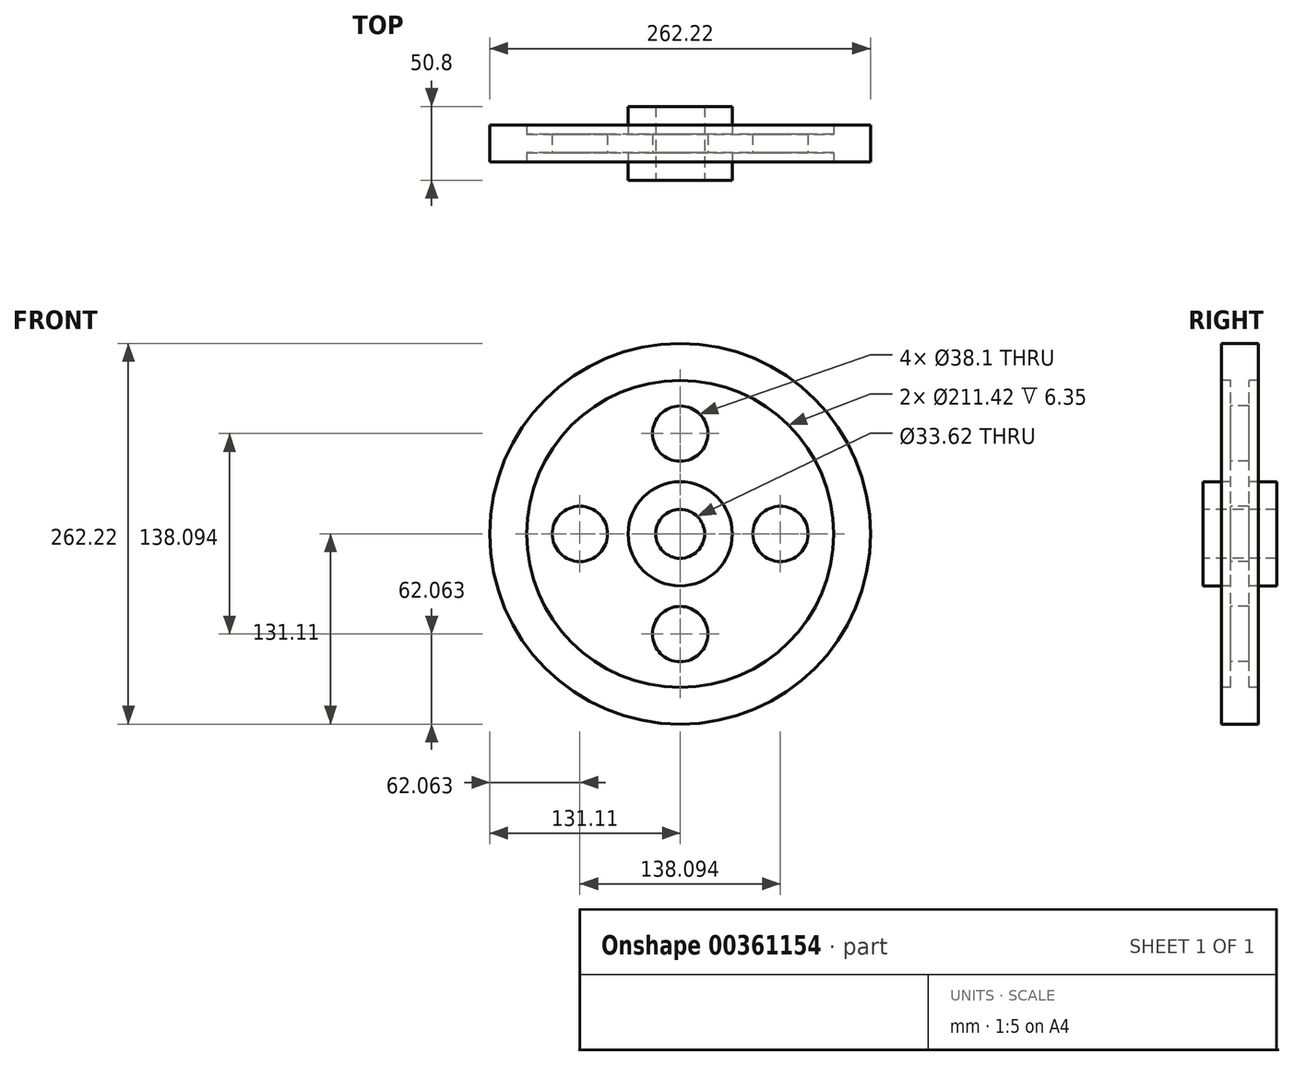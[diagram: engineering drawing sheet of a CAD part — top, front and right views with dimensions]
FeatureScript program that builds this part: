
annotation { "Feature Type Name" : "Feature", "Feature Type Description" : "" }
export const myFeature = defineFeature(function(context is Context, id is Id, definition is map)
    precondition{}
    {
        {
            var Q0;
            Q0=qCreatedBy(makeId("Right.planeOp"),FACE);
            var sketch = newSketch(context, id + "F0", { "sketchPlane" : qUnion([Q0])});
            skLineSegment(sketch, "E0", {"start": v(0, -2.24) * mm, "end": v(0, 26.34) * mm});
            skLineSegment(sketch, "E1", {"start": v(0, 26.34) * mm, "end": v(0, 28.78) * mm});
            skLineSegment(sketch, "E2.bottom", {"start": v(25.4, 35.86) * mm, "end": v(6.35, 35.86) * mm});
            skLineSegment(sketch, "E2.top", {"start": v(25.4, 16.81) * mm, "end": v(-25.4, 16.81) * mm});
            skLineSegment(sketch, "E2.left", {"start": v(25.4, 35.86) * mm, "end": v(25.4, 16.81) * mm});
            skLineSegment(sketch, "E2.right", {"start": v(-25.4, 35.86) * mm, "end": v(-25.4, 16.81) * mm});
            skPoint(sketch, "E2.middle", {"position": v(0, 26.34) * mm});
            skLineSegment(sketch, "E3.bottom", {"start": v(-12.7, 131.11) * mm, "end": v(12.7, 131.11) * mm});
            skLineSegment(sketch, "E3.top", {"start": v(-12.7, 105.71) * mm, "end": v(-6.35, 105.71) * mm});
            skLineSegment(sketch, "E3.left", {"start": v(-12.7, 131.11) * mm, "end": v(-12.7, 105.71) * mm});
            skLineSegment(sketch, "E3.right", {"start": v(12.7, 131.11) * mm, "end": v(12.7, 105.71) * mm});
            skPoint(sketch, "E3.middle", {"position": v(0, 118.41) * mm});
            skLineSegment(sketch, "E4.bottom", {"start": v(-6.35, 28.78) * mm, "end": v(0, 28.78) * mm});
            skLineSegment(sketch, "E4.left", {"start": v(-6.35, 28.78) * mm, "end": v(-6.35, 112.8) * mm});
            skLineSegment(sketch, "E4.right", {"start": v(6.35, 28.78) * mm, "end": v(6.35, 112.8) * mm});
            skPoint(sketch, "E4.middle", {"position": v(0, 70.79) * mm});
            skLineSegment(sketch, "E5.trimOffspring", {"start": v(6.35, 105.71) * mm, "end": v(12.7, 105.71) * mm});
            skLineSegment(sketch, "E6.trimOffspring", {"start": v(-6.35, 35.86) * mm, "end": v(-25.4, 35.86) * mm});
            skLineSegment(sketch, "E7", {"start": v(0, 0) * mm, "end": v(36.9, 0) * mm});
            skSolve(sketch);
        }
        {
            var Q0;
            {var subQ4=sQuery(id+"F0.wireOp",EDGE,"E1");Q0=makeQuery(id+"F0.imprint","IMPRINT",FACE,{"disambiguationData":[TD([[makeQuery(id+"F0.imprint","IMPRINT",EDGE,{"derivedFrom":subQ4}),1.0]])]});}
            var Q1;
            {var subQ3=sQuery(id+"F0.wireOp",EDGE,"E1");Q1=makeQuery(id+"F0.imprint","IMPRINT",FACE,{"disambiguationData":[TD([[makeQuery(id+"F0.imprint","IMPRINT",EDGE,{"derivedFrom":subQ3}),-1.0]])]});}
            var Q2;
            Q2=sQuery(id+"F0.wireOp",EDGE,"E7");
            revolve(context, id + "F1", {"entities" : qUnion([Q0, Q1]), "axis" : qUnion([Q2]), "revolveType" : RevolveType.FULL});
        }
        {
            var Q0;
            Q0=makeQuery(id+"F1.opRevolve","SWEPT_FACE",FACE,{"disambiguationData":[OSD([sQuery(id+"F0.wireOp",EDGE,"E4.left")])]});
            var sketch = newSketch(context, id + "F2", { "sketchPlane" : qUnion([Q0])});
            skLineSegment(sketch, "E8", {"start": v(0, -3.85) * mm, "end": v(0, 69.05) * mm});
            skCircle(sketch, "E9", {"center": v(0, 69.05) * mm, "radius": 19.05 * mm});
            skCircle(sketch, "E10.1.0", {"center": v(-69.05, 0) * mm, "radius": 19.05 * mm});
            skCircle(sketch, "E10.2.0", {"center": v(0, -69.05) * mm, "radius": 19.05 * mm});
            skCircle(sketch, "E10.3.0", {"center": v(69.05, 0) * mm, "radius": 19.05 * mm});
            skPoint(sketch, "E10.center", {"position": v(0, 0) * mm});
            skSolve(sketch);
        }
        {
            var Q0;
            Q0=makeQuery(id+"F2.imprint","IMPRINT",FACE,{"disambiguationData":[TD([[makeQuery(id+"F2.imprint","IMPRINT",EDGE,{"derivedFrom":sQuery(id+"F2.wireOp",EDGE,"E9")}),1.0]])]});
            var Q1;
            Q1=makeQuery(id+"F2.imprint","IMPRINT",FACE,{"disambiguationData":[TD([[makeQuery(id+"F2.imprint","IMPRINT",EDGE,{"derivedFrom":sQuery(id+"F2.wireOp",EDGE,"E10.3.0")}),1.0]])]});
            var Q2;
            Q2=makeQuery(id+"F2.imprint","IMPRINT",FACE,{"disambiguationData":[TD([[makeQuery(id+"F2.imprint","IMPRINT",EDGE,{"derivedFrom":sQuery(id+"F2.wireOp",EDGE,"E10.2.0")}),1.0]])]});
            var Q3;
            Q3=makeQuery(id+"F2.imprint","IMPRINT",FACE,{"disambiguationData":[TD([[makeQuery(id+"F2.imprint","IMPRINT",EDGE,{"derivedFrom":sQuery(id+"F2.wireOp",EDGE,"E10.1.0")}),1.0]])]});
            extrude(context, id + "F3", {"entities" : qUnion([Q0, Q1, Q2, Q3]), "operationType" : NewBodyOperationType.REMOVE, "oppositeDirection" : true, "depth" : 25.4 * mm});
        }
    });
